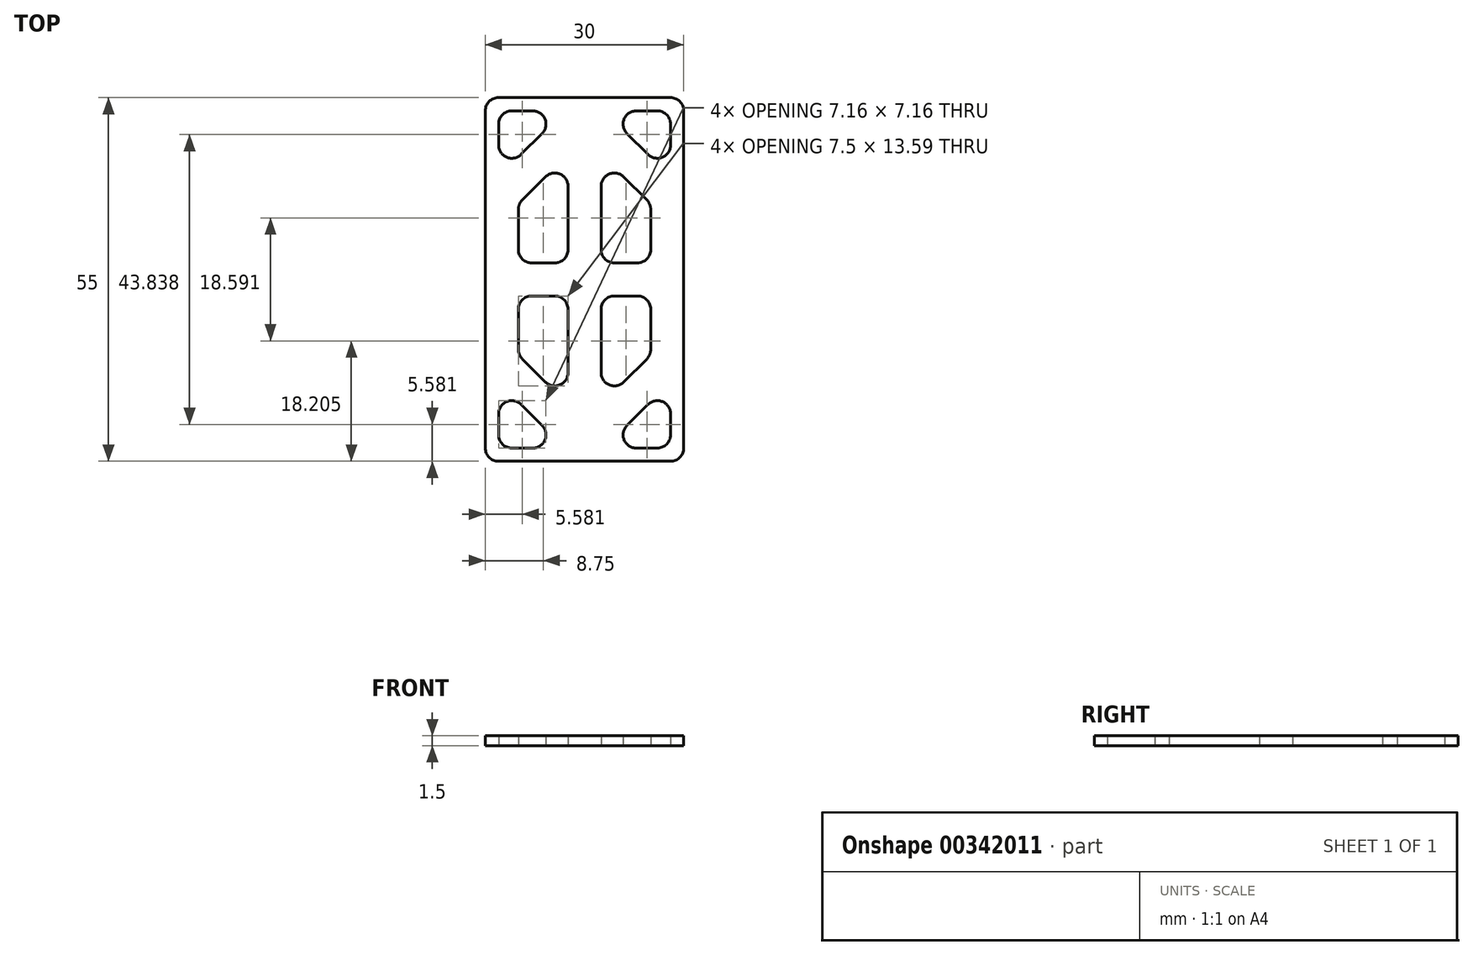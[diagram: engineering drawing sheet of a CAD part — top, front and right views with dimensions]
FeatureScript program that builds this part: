
annotation { "Feature Type Name" : "Feature", "Feature Type Description" : "" }
export const myFeature = defineFeature(function(context is Context, id is Id, definition is map)
    precondition{}
    {
        {
            var Q0;
            Q0=qCreatedBy(makeId("Top.planeOp"),FACE);
            var sketch = newSketch(context, id + "F0", { "sketchPlane" : qUnion([Q0])});
            skLineSegment(sketch, "E0.bottom", {"start": v(0, 0) * mm, "end": v(30, 0) * mm});
            skLineSegment(sketch, "E0.top", {"start": v(0, 55) * mm, "end": v(30, 55) * mm});
            skLineSegment(sketch, "E0.left", {"start": v(0, 0) * mm, "end": v(0, 55) * mm});
            skLineSegment(sketch, "E0.right", {"start": v(30, 0) * mm, "end": v(30, 55) * mm});
            skLineSegment(sketch, "E1.0", {"start": v(2, 1.97) * mm, "end": v(2, 53) * mm});
            skLineSegment(sketch, "E2.0", {"start": v(2, 53) * mm, "end": v(28, 53) * mm});
            skLineSegment(sketch, "E3.0", {"start": v(28, 1.97) * mm, "end": v(28, 53) * mm});
            skLineSegment(sketch, "E4.0", {"start": v(2, 2) * mm, "end": v(28, 2) * mm});
            skLineSegment(sketch, "E5", {"start": v(2, 43) * mm, "end": v(12, 53) * mm});
            skLineSegment(sketch, "E6", {"start": v(18, 53) * mm, "end": v(28, 43) * mm});
            skLineSegment(sketch, "E7", {"start": v(2, 12) * mm, "end": v(12, 2) * mm});
            skLineSegment(sketch, "E8", {"start": v(18, 2) * mm, "end": v(28, 12) * mm});
            skLineSegment(sketch, "E9.0", {"start": v(5, 38.93) * mm, "end": v(15, 48.93) * mm});
            skLineSegment(sketch, "E10.0", {"start": v(15, 48.93) * mm, "end": v(25, 38.93) * mm});
            skLineSegment(sketch, "E11.0", {"start": v(5, 16.07) * mm, "end": v(15, 6.07) * mm});
            skLineSegment(sketch, "E12.0", {"start": v(15, 6.07) * mm, "end": v(25, 16.07) * mm});
            skLineSegment(sketch, "E13", {"start": v(5, 38.93) * mm, "end": v(5, 30) * mm});
            skLineSegment(sketch, "E14", {"start": v(5, 30) * mm, "end": v(25, 30) * mm});
            skLineSegment(sketch, "E15", {"start": v(25, 30) * mm, "end": v(25, 38.93) * mm});
            skLineSegment(sketch, "E16", {"start": v(5, 16.07) * mm, "end": v(5, 25) * mm});
            skLineSegment(sketch, "E17", {"start": v(5, 25) * mm, "end": v(25, 25) * mm});
            skLineSegment(sketch, "E18", {"start": v(25, 25) * mm, "end": v(25, 16.07) * mm});
            skLineSegment(sketch, "E19", {"start": v(12.5, 30) * mm, "end": v(12.5, 46.43) * mm});
            skLineSegment(sketch, "E20", {"start": v(17.5, 30) * mm, "end": v(17.5, 46.43) * mm});
            skLineSegment(sketch, "E21", {"start": v(12.5, 25) * mm, "end": v(12.5, 8.57) * mm});
            skLineSegment(sketch, "E22", {"start": v(17.5, 25) * mm, "end": v(17.5, 8.57) * mm});
            skSolve(sketch);
        }
        {
            var Q0;
            Q0=makeQuery(id+"F0.imprint","IMPRINT",FACE,{"disambiguationData":[TD([[makeQuery(id+"F0.imprint","IMPRINT",EDGE,{"derivedFrom":sQuery(id+"F0.wireOp",EDGE,"E0.bottom")}),1.0]])]});
            var Q1;
            {var subQ25=sQuery(id+"F0.wireOp",EDGE,"E5");Q1=makeQuery(id+"F0.imprint","IMPRINT",FACE,{"disambiguationData":[TD([[makeQuery(id+"F0.imprint","IMPRINT",EDGE,{"derivedFrom":subQ25}),-1.0]])]});}
            var Q2;
            {var subQ0=sQuery(id+"F0.wireOp",EDGE,"E19");Q2=makeQuery(id+"F0.imprint","IMPRINT",FACE,{"disambiguationData":[TD([[makeQuery(id+"F0.imprint","IMPRINT",EDGE,{"derivedFrom":subQ0}),-1.0]])]});}
            var Q3;
            {var subQ4=sQuery(id+"F0.wireOp",EDGE,"E21");Q3=makeQuery(id+"F0.imprint","IMPRINT",FACE,{"disambiguationData":[TD([[makeQuery(id+"F0.imprint","IMPRINT",EDGE,{"derivedFrom":subQ4}),1.0]])]});}
            extrude(context, id + "F1", {"entities" : qUnion([Q0, Q1, Q2, Q3]), "depth" : 1.5 * mm});
        }
        {
            var Q0;
            Q0=makeQuery(id+"F1.opExtrude","SWEPT_EDGE",EDGE,{"disambiguationData":[OSD([sQuery(id+"F0.wireOp",EDGE,"E1.0"),sQuery(id+"F0.wireOp",EDGE,"E2.0")])]});
            var Q1;
            Q1=makeQuery(id+"F1.opExtrude","SWEPT_EDGE",EDGE,{"disambiguationData":[OSD([sQuery(id+"F0.wireOp",EDGE,"E2.0"),sQuery(id+"F0.wireOp",EDGE,"E5")])]});
            var Q2;
            Q2=makeQuery(id+"F1.opExtrude","SWEPT_EDGE",EDGE,{"disambiguationData":[OSD([sQuery(id+"F0.wireOp",EDGE,"E1.0"),sQuery(id+"F0.wireOp",EDGE,"E5")])]});
            var Q3;
            Q3=makeQuery(id+"F1.opExtrude","SWEPT_EDGE",EDGE,{"disambiguationData":[OSD([sQuery(id+"F0.wireOp",EDGE,"E0.top"),sQuery(id+"F0.wireOp",EDGE,"E0.left")])]});
            var Q4;
            Q4=makeQuery(id+"F1.opExtrude","SWEPT_EDGE",EDGE,{"disambiguationData":[OSD([sQuery(id+"F0.wireOp",EDGE,"E0.top"),sQuery(id+"F0.wireOp",EDGE,"E0.right")])]});
            var Q5;
            Q5=makeQuery(id+"F1.opExtrude","SWEPT_EDGE",EDGE,{"disambiguationData":[OSD([sQuery(id+"F0.wireOp",EDGE,"E0.bottom"),sQuery(id+"F0.wireOp",EDGE,"E0.right")])]});
            var Q6;
            Q6=makeQuery(id+"F1.opExtrude","SWEPT_EDGE",EDGE,{"disambiguationData":[OSD([sQuery(id+"F0.wireOp",EDGE,"E0.bottom"),sQuery(id+"F0.wireOp",EDGE,"E0.left")])]});
            var Q7;
            Q7=makeQuery(id+"F1.opExtrude","SWEPT_EDGE",EDGE,{"disambiguationData":[OSD([sQuery(id+"F0.wireOp",EDGE,"E2.0"),sQuery(id+"F0.wireOp",EDGE,"E3.0")])]});
            var Q8;
            Q8=makeQuery(id+"F1.opExtrude","SWEPT_EDGE",EDGE,{"disambiguationData":[OSD([sQuery(id+"F0.wireOp",EDGE,"E2.0"),sQuery(id+"F0.wireOp",EDGE,"E6")])]});
            var Q9;
            Q9=makeQuery(id+"F1.opExtrude","SWEPT_EDGE",EDGE,{"disambiguationData":[OSD([sQuery(id+"F0.wireOp",EDGE,"E3.0"),sQuery(id+"F0.wireOp",EDGE,"E6")])]});
            var Q10;
            Q10=makeQuery(id+"F1.opExtrude","SWEPT_EDGE",EDGE,{"disambiguationData":[OSD([sQuery(id+"F0.wireOp",EDGE,"E14"),sQuery(id+"F0.wireOp",EDGE,"E15")])]});
            var Q11;
            Q11=makeQuery(id+"F1.opExtrude","SWEPT_EDGE",EDGE,{"disambiguationData":[OSD([sQuery(id+"F0.wireOp",EDGE,"E14"),sQuery(id+"F0.wireOp",EDGE,"E20")])]});
            var Q12;
            Q12=makeQuery(id+"F1.opExtrude","SWEPT_EDGE",EDGE,{"disambiguationData":[OSD([sQuery(id+"F0.wireOp",EDGE,"E10.0"),sQuery(id+"F0.wireOp",EDGE,"E20")])]});
            var Q13;
            Q13=makeQuery(id+"F1.opExtrude","SWEPT_EDGE",EDGE,{"disambiguationData":[OSD([sQuery(id+"F0.wireOp",EDGE,"E10.0"),sQuery(id+"F0.wireOp",EDGE,"E15")])]});
            var Q14;
            Q14=makeQuery(id+"F1.opExtrude","SWEPT_EDGE",EDGE,{"disambiguationData":[OSD([sQuery(id+"F0.wireOp",EDGE,"E9.0"),sQuery(id+"F0.wireOp",EDGE,"E19")])]});
            var Q15;
            Q15=makeQuery(id+"F1.opExtrude","SWEPT_EDGE",EDGE,{"disambiguationData":[OSD([sQuery(id+"F0.wireOp",EDGE,"E9.0"),sQuery(id+"F0.wireOp",EDGE,"E13")])]});
            var Q16;
            Q16=makeQuery(id+"F1.opExtrude","SWEPT_EDGE",EDGE,{"disambiguationData":[OSD([sQuery(id+"F0.wireOp",EDGE,"E13"),sQuery(id+"F0.wireOp",EDGE,"E14")])]});
            var Q17;
            Q17=makeQuery(id+"F1.opExtrude","SWEPT_EDGE",EDGE,{"disambiguationData":[OSD([sQuery(id+"F0.wireOp",EDGE,"E14"),sQuery(id+"F0.wireOp",EDGE,"E19")])]});
            var Q18;
            Q18=makeQuery(id+"F1.opExtrude","SWEPT_EDGE",EDGE,{"disambiguationData":[OSD([sQuery(id+"F0.wireOp",EDGE,"E11.0"),sQuery(id+"F0.wireOp",EDGE,"E21")])]});
            var Q19;
            Q19=makeQuery(id+"F1.opExtrude","SWEPT_EDGE",EDGE,{"disambiguationData":[OSD([sQuery(id+"F0.wireOp",EDGE,"E11.0"),sQuery(id+"F0.wireOp",EDGE,"E16")])]});
            var Q20;
            Q20=makeQuery(id+"F1.opExtrude","SWEPT_EDGE",EDGE,{"disambiguationData":[OSD([sQuery(id+"F0.wireOp",EDGE,"E16"),sQuery(id+"F0.wireOp",EDGE,"E17")])]});
            var Q21;
            Q21=makeQuery(id+"F1.opExtrude","SWEPT_EDGE",EDGE,{"disambiguationData":[OSD([sQuery(id+"F0.wireOp",EDGE,"E17"),sQuery(id+"F0.wireOp",EDGE,"E21")])]});
            var Q22;
            Q22=makeQuery(id+"F1.opExtrude","SWEPT_EDGE",EDGE,{"disambiguationData":[OSD([sQuery(id+"F0.wireOp",EDGE,"E17"),sQuery(id+"F0.wireOp",EDGE,"E18")])]});
            var Q23;
            Q23=makeQuery(id+"F1.opExtrude","SWEPT_EDGE",EDGE,{"disambiguationData":[OSD([sQuery(id+"F0.wireOp",EDGE,"E12.0"),sQuery(id+"F0.wireOp",EDGE,"E18")])]});
            var Q24;
            Q24=makeQuery(id+"F1.opExtrude","SWEPT_EDGE",EDGE,{"disambiguationData":[OSD([sQuery(id+"F0.wireOp",EDGE,"E17"),sQuery(id+"F0.wireOp",EDGE,"E22")])]});
            var Q25;
            Q25=makeQuery(id+"F1.opExtrude","SWEPT_EDGE",EDGE,{"disambiguationData":[OSD([sQuery(id+"F0.wireOp",EDGE,"E12.0"),sQuery(id+"F0.wireOp",EDGE,"E22")])]});
            var Q26;
            Q26=makeQuery(id+"F1.opExtrude","SWEPT_EDGE",EDGE,{"disambiguationData":[OSD([sQuery(id+"F0.wireOp",EDGE,"E1.0"),sQuery(id+"F0.wireOp",EDGE,"E4.0")])]});
            var Q27;
            Q27=makeQuery(id+"F1.opExtrude","SWEPT_EDGE",EDGE,{"disambiguationData":[OSD([sQuery(id+"F0.wireOp",EDGE,"E1.0"),sQuery(id+"F0.wireOp",EDGE,"E7")])]});
            var Q28;
            Q28=makeQuery(id+"F1.opExtrude","SWEPT_EDGE",EDGE,{"disambiguationData":[OSD([sQuery(id+"F0.wireOp",EDGE,"E4.0"),sQuery(id+"F0.wireOp",EDGE,"E7")])]});
            var Q29;
            Q29=makeQuery(id+"F1.opExtrude","SWEPT_EDGE",EDGE,{"disambiguationData":[OSD([sQuery(id+"F0.wireOp",EDGE,"E3.0"),sQuery(id+"F0.wireOp",EDGE,"E8")])]});
            var Q30;
            Q30=makeQuery(id+"F1.opExtrude","SWEPT_EDGE",EDGE,{"disambiguationData":[OSD([sQuery(id+"F0.wireOp",EDGE,"E3.0"),sQuery(id+"F0.wireOp",EDGE,"E4.0")])]});
            var Q31;
            Q31=makeQuery(id+"F1.opExtrude","SWEPT_EDGE",EDGE,{"disambiguationData":[OSD([sQuery(id+"F0.wireOp",EDGE,"E4.0"),sQuery(id+"F0.wireOp",EDGE,"E8")])]});
            fillet(context, id + "F2", {"entities" : qUnion([Q0, Q1, Q2, Q3, Q4, Q5, Q6, Q7, Q8, Q9, Q10, Q11, Q12, Q13, Q14, Q15, Q16, Q17, Q18, Q19, Q20, Q21, Q22, Q23, Q24, Q25, Q26, Q27, Q28, Q29, Q30, Q31]), "radius" : 2 * mm, "tangentPropagation" : true, "allowEdgeOverflow" : false});
        }
    });
